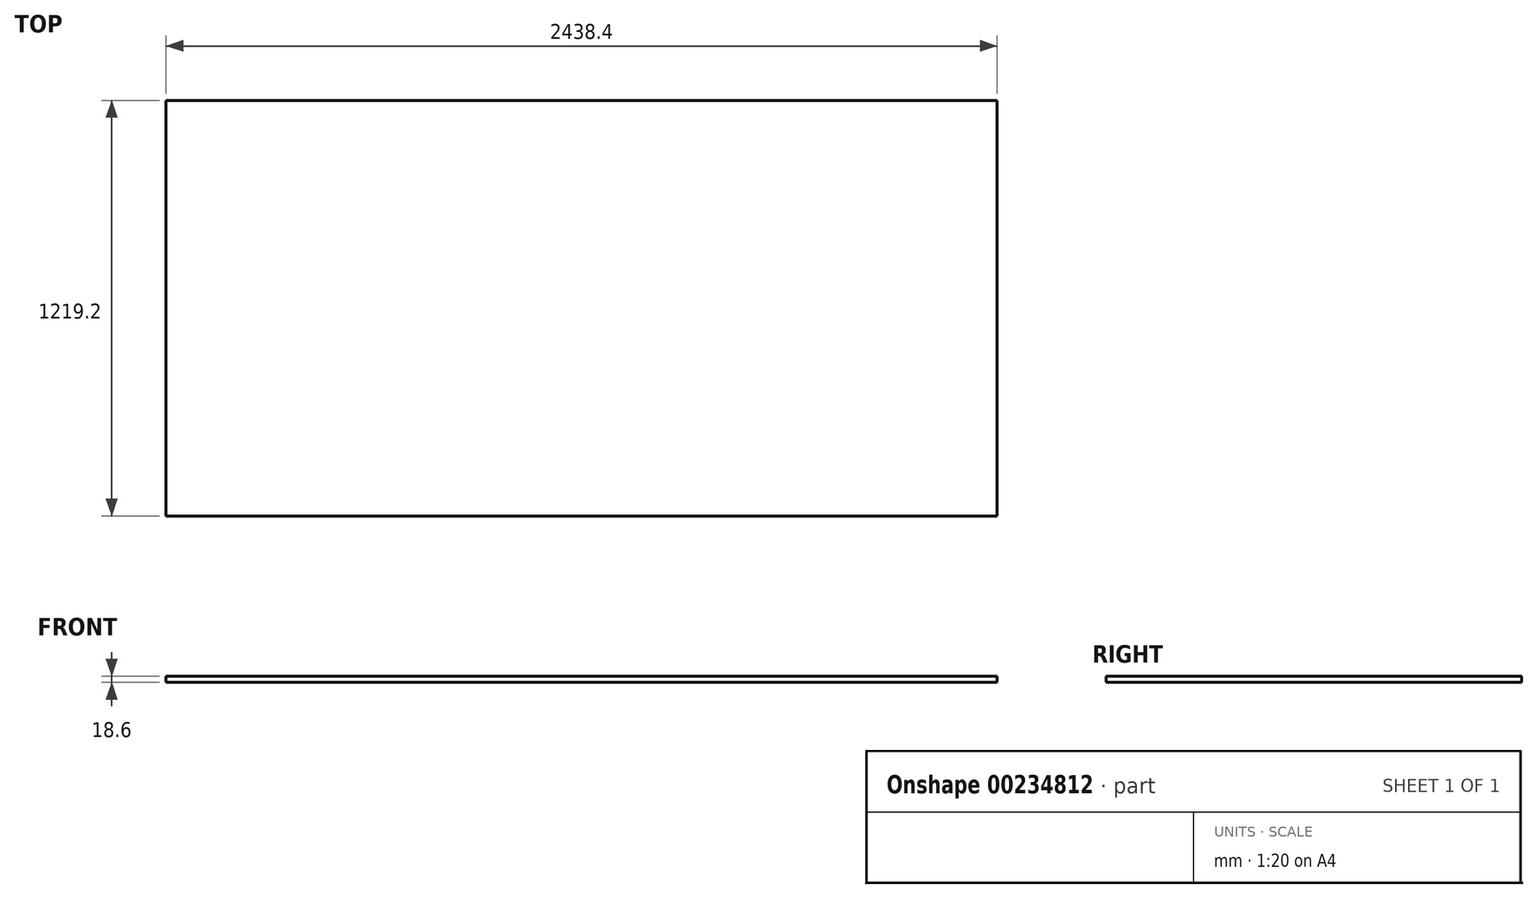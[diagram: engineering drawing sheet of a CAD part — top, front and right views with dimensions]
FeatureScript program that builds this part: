
annotation { "Feature Type Name" : "Feature", "Feature Type Description" : "" }
export const myFeature = defineFeature(function(context is Context, id is Id, definition is map)
    precondition{}
    {
        {
            var Q0;
            Q0=qCreatedBy(makeId("Top.planeOp"),FACE);
            var sketch = newSketch(context, id + "F0", { "sketchPlane" : qUnion([Q0])});
            skLineSegment(sketch, "E0.bottom", {"start": v(1219.2, 609.6) * mm, "end": v(-1219.2, 609.6) * mm});
            skLineSegment(sketch, "E0.top", {"start": v(1219.2, -609.6) * mm, "end": v(-1219.2, -609.6) * mm});
            skLineSegment(sketch, "E0.left", {"start": v(1219.2, 609.6) * mm, "end": v(1219.2, -609.6) * mm});
            skLineSegment(sketch, "E0.right", {"start": v(-1219.2, 609.6) * mm, "end": v(-1219.2, -609.6) * mm});
            skPoint(sketch, "E0.middle", {"position": v(0, 0) * mm});
            skSolve(sketch);
        }
        {
            var Q0;
            Q0 = qSketchRegion(id + "F0", true);
            extrude(context, id + "F1", {"entities" : qUnion([Q0]), "depth" : 18.6 * mm, "offsetDistance" : 25 * mm});
        }
    });
